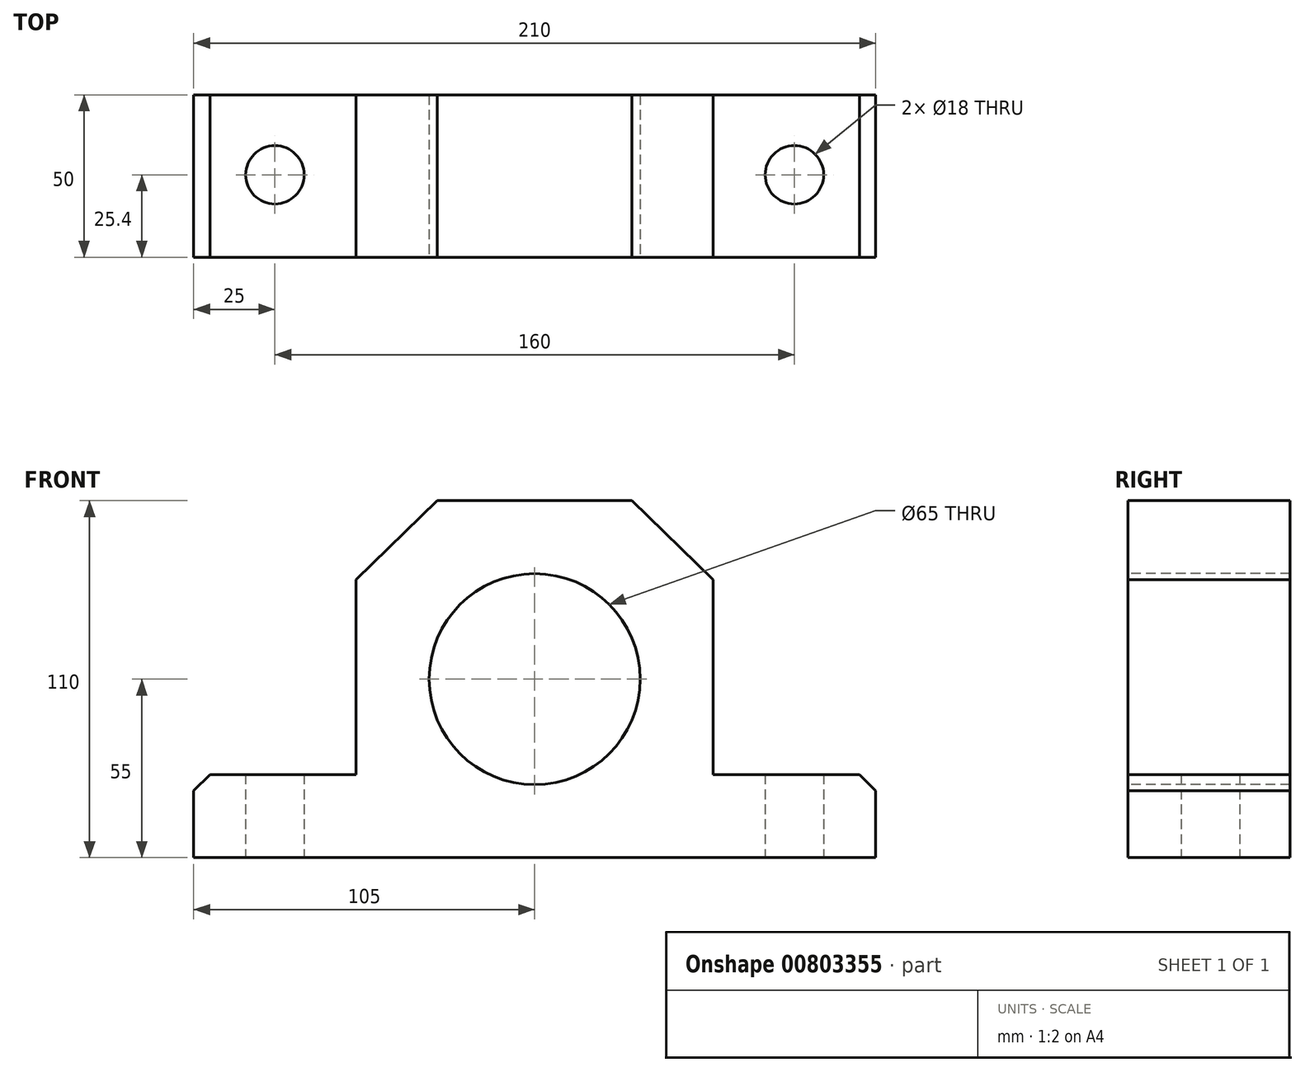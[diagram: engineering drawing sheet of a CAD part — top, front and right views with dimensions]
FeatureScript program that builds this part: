
annotation { "Feature Type Name" : "Feature", "Feature Type Description" : "" }
export const myFeature = defineFeature(function(context is Context, id is Id, definition is map)
    precondition{}
    {
        {
            var Q0;
            Q0=qCreatedBy(makeId("Front.planeOp"),FACE);
            var sketch = newSketch(context, id + "F0", { "sketchPlane" : qUnion([Q0])});
            skCircle(sketch, "E0", {"center": v(0, 0) * mm, "radius": 32.5 * mm});
            skLineSegment(sketch, "E1", {"start": v(0, 55) * mm, "end": v(-30, 55) * mm});
            skLineSegment(sketch, "E2", {"start": v(-30, 55) * mm, "end": v(-55, 30.6) * mm});
            skLineSegment(sketch, "E3", {"start": v(-55, 30.6) * mm, "end": v(-55, -29.4) * mm});
            skLineSegment(sketch, "E4", {"start": v(-55, -29.4) * mm, "end": v(-105, -29.4) * mm});
            skLineSegment(sketch, "E5", {"start": v(-105, -29.4) * mm, "end": v(-105, -55) * mm});
            skLineSegment(sketch, "E6", {"start": v(-105, -55) * mm, "end": v(0, -55) * mm});
            skLineSegment(sketch, "E7.MirrorCS", {"start": v(0, 55) * mm, "end": v(30, 55) * mm});
            skLineSegment(sketch, "E8.MirrorCS", {"start": v(30, 55) * mm, "end": v(55, 30.6) * mm});
            skLineSegment(sketch, "E9.MirrorCS", {"start": v(55, 30.6) * mm, "end": v(55, -29.4) * mm});
            skLineSegment(sketch, "E10.MirrorCS", {"start": v(55, -29.4) * mm, "end": v(105, -29.4) * mm});
            skLineSegment(sketch, "E11.MirrorCS", {"start": v(105, -55) * mm, "end": v(0, -55) * mm});
            skLineSegment(sketch, "E12.MirrorCS", {"start": v(105, -29.4) * mm, "end": v(105, -55) * mm});
            skSolve(sketch);
        }
        {
            var Q0;
            Q0=makeQuery(id+"F0.imprint","IMPRINT",FACE,{"disambiguationData":[TD([[makeQuery(id+"F0.imprint","IMPRINT",EDGE,{"derivedFrom":sQuery(id+"F0.wireOp",EDGE,"E0")}),-1.0]])]});
            extrude(context, id + "F1", {"entities" : qUnion([Q0]), "oppositeDirection" : true, "depth" : 50 * mm, "offsetDistance" : 25 * mm});
        }
        {
            var Q0;
            Q0=makeQuery(id+"F1.opExtrude","SWEPT_EDGE",EDGE,{"disambiguationData":[OSD([sQuery(id+"F0.wireOp",EDGE,"E10.MirrorCS"),sQuery(id+"F0.wireOp",EDGE,"E12.MirrorCS")])]});
            var Q1;
            Q1=makeQuery(id+"F1.opExtrude","SWEPT_EDGE",EDGE,{"disambiguationData":[OSD([sQuery(id+"F0.wireOp",EDGE,"E4"),sQuery(id+"F0.wireOp",EDGE,"E5")])]});
            chamfer(context, id + "F2", {"entities" : qUnion([Q0, Q1]), "width" : 5 * mm, "tangentPropagation" : true});
        }
        {
            var Q0;
            Q0=makeQuery(id+"F1.opExtrude","SWEPT_FACE",FACE,{"disambiguationData":[OSD([sQuery(id+"F0.wireOp",EDGE,"E6"),sQuery(id+"F0.wireOp",EDGE,"E11.MirrorCS")])]});
            var sketch = newSketch(context, id + "F3", { "sketchPlane" : qUnion([Q0])});
            skPoint(sketch, "E13", {"position": v(-80, -25.4) * mm});
            skPoint(sketch, "E14.MirrorP", {"position": v(80, -25.4) * mm});
            skSolve(sketch);
        }
        {
            var Q0;
            Q0=sQuery(id+"F3.wireOp",VERTEX,"E13");
            var Q1;
            Q1=sQuery(id+"F3.wireOp",VERTEX,"E14.MirrorP");
            var Q2;
            Q2=makeQuery(id+"F1.opExtrude","SWEPT_BODY",BODY,{"disambiguationData":[OSD([sQuery(id+"F0.wireOp",EDGE,"E0"),sQuery(id+"F0.wireOp",EDGE,"E1"),sQuery(id+"F0.wireOp",EDGE,"E2"),sQuery(id+"F0.wireOp",EDGE,"E3"),sQuery(id+"F0.wireOp",EDGE,"E4"),sQuery(id+"F0.wireOp",EDGE,"E5"),sQuery(id+"F0.wireOp",EDGE,"E6"),sQuery(id+"F0.wireOp",EDGE,"E7.MirrorCS"),sQuery(id+"F0.wireOp",EDGE,"E8.MirrorCS"),sQuery(id+"F0.wireOp",EDGE,"E9.MirrorCS"),sQuery(id+"F0.wireOp",EDGE,"E10.MirrorCS"),sQuery(id+"F0.wireOp",EDGE,"E11.MirrorCS"),sQuery(id+"F0.wireOp",EDGE,"E12.MirrorCS")])]});
            hole(context, id + "F4", {"style" : HoleStyle.SIMPLE, "endStyle" : HoleEndStyle.THROUGH, "holeDiameter" : 18 * mm, "majorDiameter" : 5 * mm, "isTappedThrough" : true, "tappedDepth" : 12 * mm, "tapClearance" : 3, "locations" : qUnion([Q0, Q1]), "scope" : qUnion([Q2])});
        }
    });
